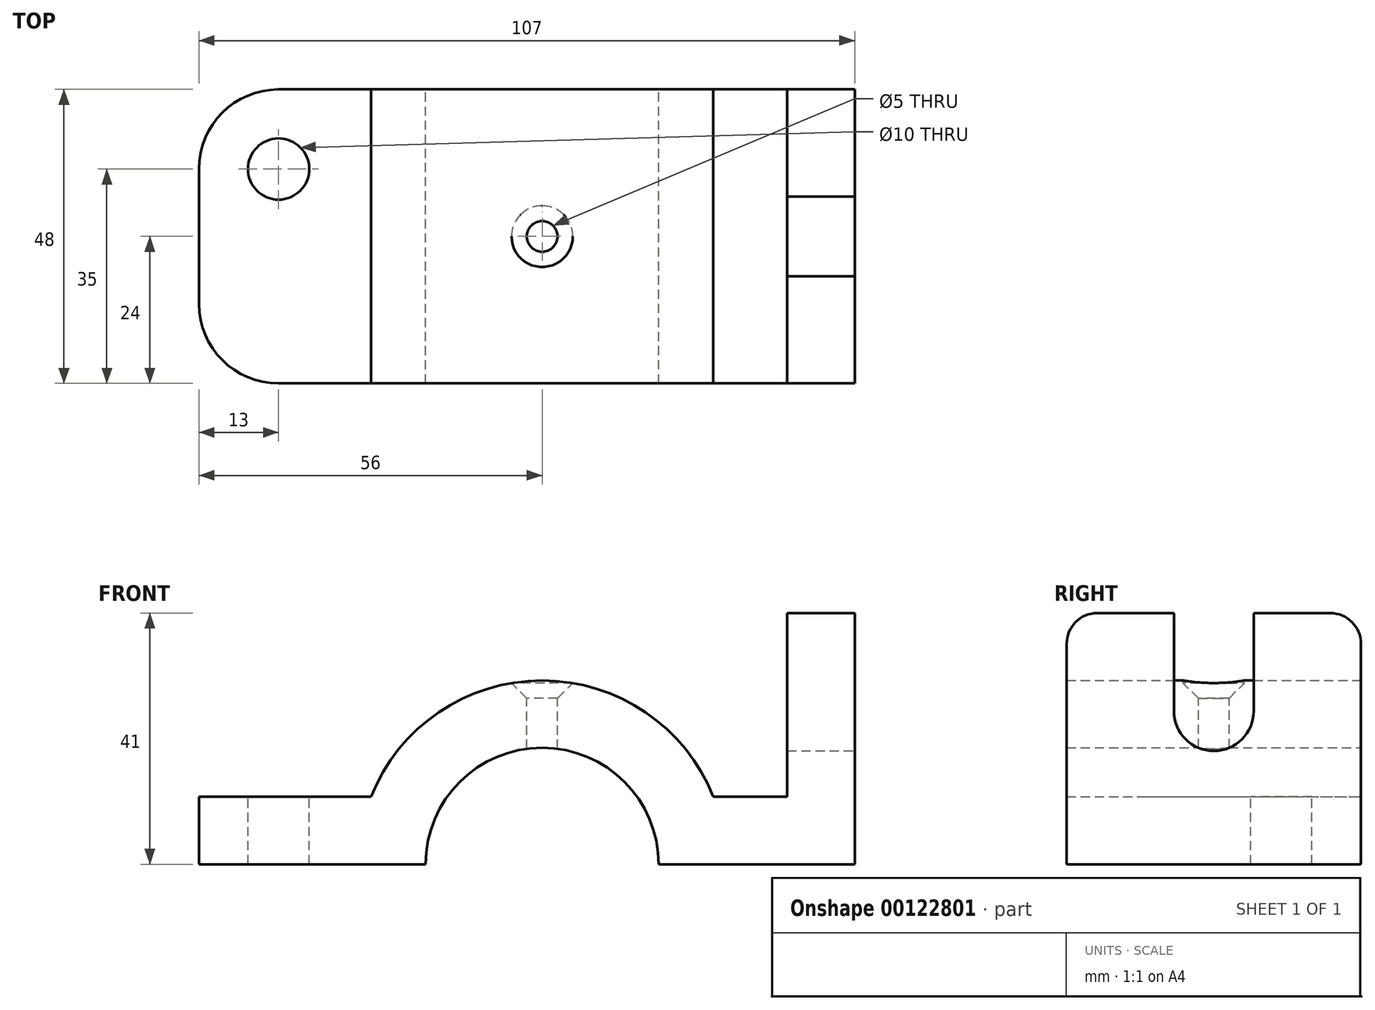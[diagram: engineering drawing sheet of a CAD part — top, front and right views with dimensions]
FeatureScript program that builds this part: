
annotation { "Feature Type Name" : "Feature", "Feature Type Description" : "" }
export const myFeature = defineFeature(function(context is Context, id is Id, definition is map)
    precondition{}
    {
        {
            var Q0;
            Q0=qCreatedBy(makeId("Front.planeOp"),FACE);
            var sketch = newSketch(context, id + "F0", { "sketchPlane" : qUnion([Q0])});
            skLineSegment(sketch, "E0", {"start": v(51, 41) * mm, "end": v(51, 0) * mm});
            skLineSegment(sketch, "E1", {"start": v(51, 0) * mm, "end": v(19, 0) * mm});
            skArc(sketch, "E2", {"start": v(19, 0) * mm, "mid": v(0, 19) * mm, "end": v(-19, 0) * mm});
            skLineSegment(sketch, "E3.trimOffspring", {"start": v(-19, 0) * mm, "end": v(-56, 0) * mm});
            skLineSegment(sketch, "E4.0", {"start": v(-27.91, 11) * mm, "end": v(-56, 11) * mm});
            skArc(sketch, "E4.1", {"start": v(27.91, 11) * mm, "mid": v(0, 30) * mm, "end": v(-27.91, 11) * mm});
            skLineSegment(sketch, "E4.2", {"start": v(40, 11) * mm, "end": v(27.91, 11) * mm});
            skLineSegment(sketch, "E4.3", {"start": v(40, 41) * mm, "end": v(40, 11) * mm});
            skLineSegment(sketch, "E5", {"start": v(40, 41) * mm, "end": v(51, 41) * mm});
            skLineSegment(sketch, "E6", {"start": v(-56, 11) * mm, "end": v(-56, 0) * mm});
            skSolve(sketch);
        }
        {
            var Q0;
            Q0 = qSketchRegion(id + "F0", true);
            extrude(context, id + "F1", {"entities" : qUnion([Q0]), "endBound" : BoundingType.SYMMETRIC, "depth" : 48 * mm});
        }
        {
            var Q0;
            Q0=makeQuery(id+"F1.opExtrude","SWEPT_FACE",FACE,{"disambiguationData":[OSD([sQuery(id+"F0.wireOp",EDGE,"E0")])]});
            var sketch = newSketch(context, id + "F2", { "sketchPlane" : qUnion([Q0])});
            skArc(sketch, "E7", {"start": v(-6.5, 25) * mm, "mid": v(0, 18.5) * mm, "end": v(6.5, 25) * mm});
            skLineSegment(sketch, "E8", {"start": v(6.5, 25) * mm, "end": v(6.5, 41) * mm});
            skLineSegment(sketch, "E9", {"start": v(-6.5, 25) * mm, "end": v(-6.5, 41) * mm});
            skLineSegment(sketch, "E10", {"start": v(-6.5, 41) * mm, "end": v(6.5, 41) * mm});
            skSolve(sketch);
        }
        {
            var Q0;
            Q0 = qSketchRegion(id + "F2", true);
            extrude(context, id + "F3", {"entities" : qUnion([Q0]), "operationType" : NewBodyOperationType.REMOVE, "oppositeDirection" : true, "depth" : 25 * mm});
        }
        {
            var Q0;
            Q0=makeQuery(id+"F1.opExtrude","CAP_EDGE",EDGE,{"disambiguationData":[OSD([sQuery(id+"F0.wireOp",EDGE,"E5")])],"isStart":true});
            var Q1;
            Q1=makeQuery(id+"F1.opExtrude","CAP_EDGE",EDGE,{"disambiguationData":[OSD([sQuery(id+"F0.wireOp",EDGE,"E5")])],"isStart":false});
            fillet(context, id + "F4", {"entities" : qUnion([Q0, Q1]), "radius" : 5 * mm, "tangentPropagation" : true, "allowEdgeOverflow" : false});
        }
        {
            var Q0;
            Q0=makeQuery(id+"F1.opExtrude","CAP_EDGE",EDGE,{"disambiguationData":[OSD([sQuery(id+"F0.wireOp",EDGE,"E6")])],"isStart":true});
            var Q1;
            Q1=makeQuery(id+"F1.opExtrude","CAP_EDGE",EDGE,{"disambiguationData":[OSD([sQuery(id+"F0.wireOp",EDGE,"E6")])],"isStart":false});
            fillet(context, id + "F5", {"entities" : qUnion([Q0, Q1]), "radius" : 13 * mm, "tangentPropagation" : true, "allowEdgeOverflow" : false});
        }
        {
            var Q0;
            Q0=qCreatedBy(makeId("Top.planeOp"),FACE);
            cPlane(context, id + "F6", {"entities" : qUnion([Q0]), "cplaneType" : CPlaneType.OFFSET, "offset" : 30 * mm, "width" : 150 * mm, "height" : 150 * mm});
        }
        {
            var Q0;
            Q0=qCreatedBy(id+"F6.planeOp",FACE);
            var sketch = newSketch(context, id + "F7", { "sketchPlane" : qUnion([Q0])});
            skPoint(sketch, "E11", {"position": v(0, 0) * mm});
            skArc(sketch, "E12.0", {"start": v(-43, 24) * mm, "mid": v(-52.2, 20.2) * mm, "end": v(-56, 11) * mm, "construction": true});
            skArc(sketch, "E13.0", {"start": v(-56, -11) * mm, "mid": v(-52.2, -20.2) * mm, "end": v(-43, -24) * mm, "construction": true});
            skSolve(sketch);
        }
        {
            var Q0;
            Q0=sQuery(id+"F7.wireOp",VERTEX,"E11");
            var Q1;
            Q1=makeQuery(id+"F1.opExtrude","SWEPT_BODY",BODY,{"disambiguationData":[OSD([sQuery(id+"F0.wireOp",EDGE,"E0"),sQuery(id+"F0.wireOp",EDGE,"E1"),sQuery(id+"F0.wireOp",EDGE,"E2"),sQuery(id+"F0.wireOp",EDGE,"E3.trimOffspring"),sQuery(id+"F0.wireOp",EDGE,"E4.0"),sQuery(id+"F0.wireOp",EDGE,"E4.1"),sQuery(id+"F0.wireOp",EDGE,"E4.2"),sQuery(id+"F0.wireOp",EDGE,"E4.3"),sQuery(id+"F0.wireOp",EDGE,"E5"),sQuery(id+"F0.wireOp",EDGE,"E6")])]});
            hole(context, id + "F8", {"style" : HoleStyle.C_SINK, "endStyle" : HoleEndStyle.THROUGH, "holeDiameter" : 5 * mm, "cSinkDiameter" : 10 * mm, "cSinkAngle" : 90 * degree, "locations" : qUnion([Q0]), "scope" : qUnion([Q1]), "isTappedThrough" : true});
        }
        {
            var Q0;
            Q0=sQuery(id+"F7.wireOp",VERTEX,"E12.0.center");
            var Q1;
            Q1=makeQuery(id+"F1.opExtrude","SWEPT_BODY",BODY,{"disambiguationData":[OSD([sQuery(id+"F0.wireOp",EDGE,"E0"),sQuery(id+"F0.wireOp",EDGE,"E1"),sQuery(id+"F0.wireOp",EDGE,"E2"),sQuery(id+"F0.wireOp",EDGE,"E3.trimOffspring"),sQuery(id+"F0.wireOp",EDGE,"E4.0"),sQuery(id+"F0.wireOp",EDGE,"E4.1"),sQuery(id+"F0.wireOp",EDGE,"E4.2"),sQuery(id+"F0.wireOp",EDGE,"E4.3"),sQuery(id+"F0.wireOp",EDGE,"E5"),sQuery(id+"F0.wireOp",EDGE,"E6")])]});
            hole(context, id + "F9", {"style" : HoleStyle.SIMPLE, "endStyle" : HoleEndStyle.THROUGH, "holeDiameter" : 10 * mm, "locations" : qUnion([Q0]), "scope" : qUnion([Q1]), "isTappedThrough" : true});
        }
    });
